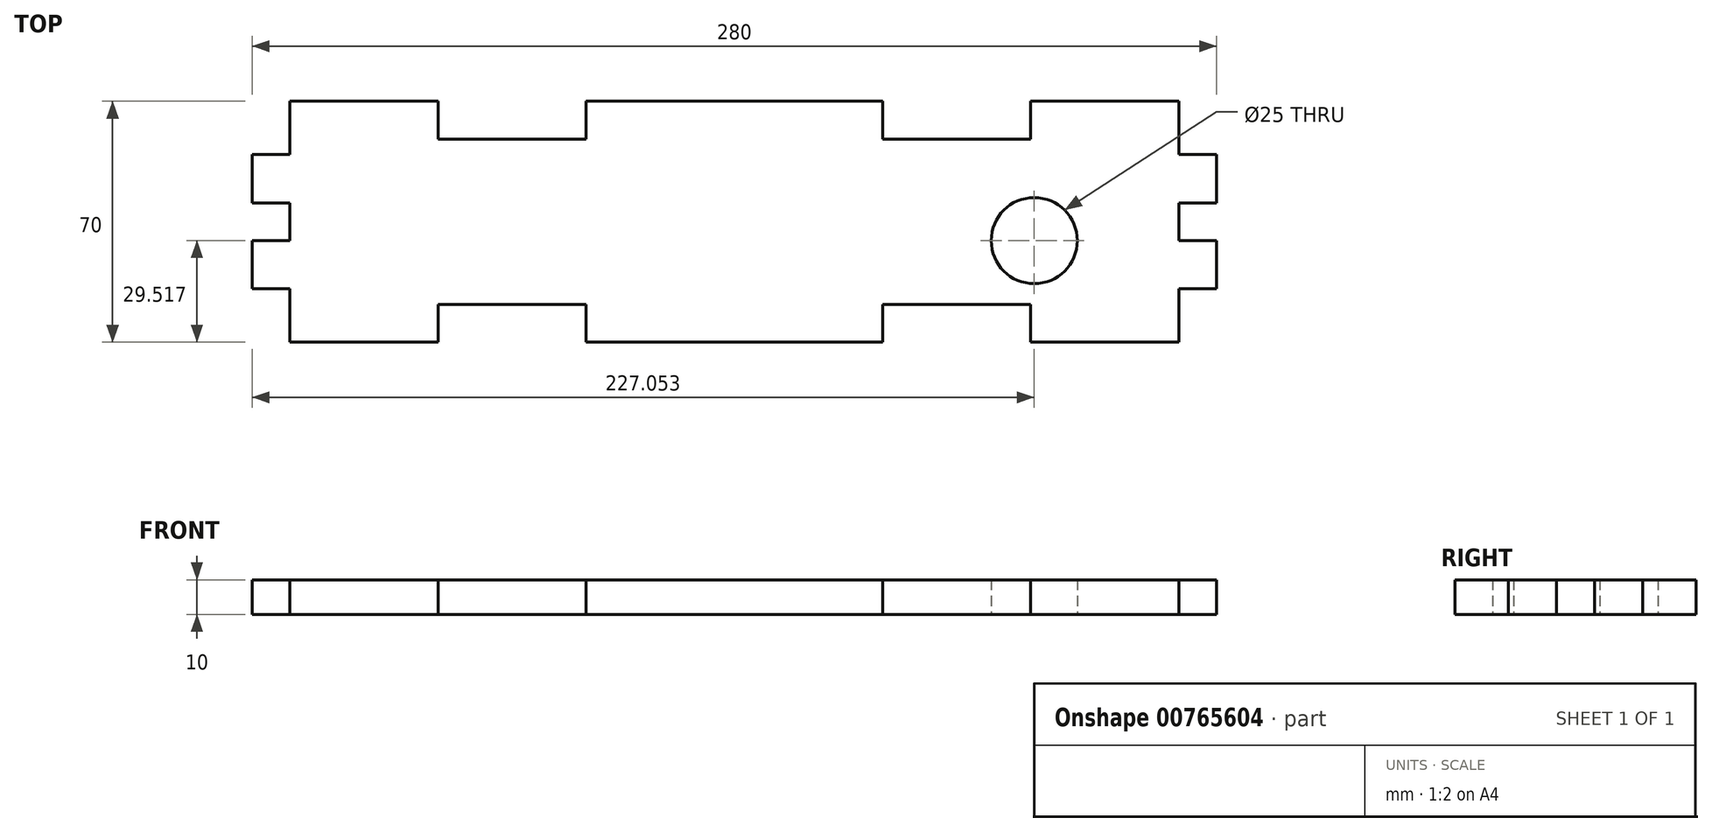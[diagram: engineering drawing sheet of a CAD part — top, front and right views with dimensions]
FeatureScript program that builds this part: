
annotation { "Feature Type Name" : "Feature", "Feature Type Description" : "" }
export const myFeature = defineFeature(function(context is Context, id is Id, definition is map)
    precondition{}
    {
        {
            var Q0;
            Q0=qCreatedBy(makeId("Top.planeOp"),FACE);
            var sketch = newSketch(context, id + "F0", { "sketchPlane" : qUnion([Q0])});
            skPoint(sketch, "E0.middle", {"position": v(0, 0) * mm});
            skLineSegment(sketch, "E1", {"start": v(129, 35) * mm, "end": v(129, 19.5) * mm});
            skLineSegment(sketch, "E2", {"start": v(129, 19.5) * mm, "end": v(140, 19.5) * mm});
            skLineSegment(sketch, "E3", {"start": v(140, 19.5) * mm, "end": v(140, 5.5) * mm});
            skLineSegment(sketch, "E4.MirrorCS", {"start": v(129, -35) * mm, "end": v(129, -19.5) * mm});
            skLineSegment(sketch, "E5.MirrorCS", {"start": v(129, -19.5) * mm, "end": v(140, -19.5) * mm});
            skLineSegment(sketch, "E6.MirrorCS", {"start": v(140, -19.5) * mm, "end": v(140, -5.5) * mm});
            skLineSegment(sketch, "E7", {"start": v(140, -5.5) * mm, "end": v(129, -5.5) * mm});
            skLineSegment(sketch, "E8", {"start": v(129, -5.5) * mm, "end": v(129, 5.5) * mm});
            skLineSegment(sketch, "E9", {"start": v(129, 5.5) * mm, "end": v(140, 5.5) * mm});
            skLineSegment(sketch, "E10.MirrorCS", {"start": v(-129, 35) * mm, "end": v(-129, 19.5) * mm});
            skLineSegment(sketch, "E11.MirrorCS", {"start": v(-129, 19.5) * mm, "end": v(-140, 19.5) * mm});
            skLineSegment(sketch, "E12.MirrorCS", {"start": v(-140, 19.5) * mm, "end": v(-140, 5.5) * mm});
            skLineSegment(sketch, "E13.MirrorCS", {"start": v(-129, 5.5) * mm, "end": v(-140, 5.5) * mm});
            skLineSegment(sketch, "E14.MirrorCS", {"start": v(-129, -5.5) * mm, "end": v(-129, 5.5) * mm});
            skLineSegment(sketch, "E15.MirrorCS", {"start": v(-140, -5.5) * mm, "end": v(-129, -5.5) * mm});
            skLineSegment(sketch, "E16.MirrorCS", {"start": v(-140, -19.5) * mm, "end": v(-140, -5.5) * mm});
            skLineSegment(sketch, "E17.MirrorCS", {"start": v(-129, -19.5) * mm, "end": v(-140, -19.5) * mm});
            skLineSegment(sketch, "E18.MirrorCS", {"start": v(-129, -35) * mm, "end": v(-129, -19.5) * mm});
            skLineSegment(sketch, "E19", {"start": v(-129, 35) * mm, "end": v(-86, 35) * mm});
            skLineSegment(sketch, "E20", {"start": v(-86, 35) * mm, "end": v(-86, 24) * mm});
            skLineSegment(sketch, "E21", {"start": v(-86, 24) * mm, "end": v(-43, 24) * mm});
            skLineSegment(sketch, "E22", {"start": v(-43, 24) * mm, "end": v(-43, 35) * mm});
            skLineSegment(sketch, "E23.MirrorCS", {"start": v(86, 35) * mm, "end": v(86, 24) * mm});
            skLineSegment(sketch, "E24.MirrorCS", {"start": v(86, 24) * mm, "end": v(43, 24) * mm});
            skLineSegment(sketch, "E25", {"start": v(86, 35) * mm, "end": v(129, 35) * mm});
            skLineSegment(sketch, "E26", {"start": v(43, 24) * mm, "end": v(43, 35) * mm});
            skLineSegment(sketch, "E27", {"start": v(-43, 35) * mm, "end": v(43, 35) * mm});
            skCircle(sketch, "E28", {"center": v(87.05, -5.48) * mm, "radius": 12.5 * mm});
            skLineSegment(sketch, "E29.MirrorCS", {"start": v(-129, -35) * mm, "end": v(-86, -35) * mm});
            skLineSegment(sketch, "E30.MirrorCS", {"start": v(-86, -35) * mm, "end": v(-86, -24) * mm});
            skLineSegment(sketch, "E31.MirrorCS", {"start": v(-86, -24) * mm, "end": v(-43, -24) * mm});
            skLineSegment(sketch, "E32.MirrorCS", {"start": v(-43, -24) * mm, "end": v(-43, -35) * mm});
            skLineSegment(sketch, "E33.MirrorCS", {"start": v(-43, -35) * mm, "end": v(43, -35) * mm});
            skLineSegment(sketch, "E34.MirrorCS", {"start": v(43, -24) * mm, "end": v(43, -35) * mm});
            skLineSegment(sketch, "E35.MirrorCS", {"start": v(86, -24) * mm, "end": v(43, -24) * mm});
            skLineSegment(sketch, "E36.MirrorCS", {"start": v(86, -35) * mm, "end": v(86, -24) * mm});
            skLineSegment(sketch, "E37.MirrorCS", {"start": v(86, -35) * mm, "end": v(129, -35) * mm});
            skSolve(sketch);
        }
        {
            var Q0;
            Q0=makeQuery(id+"F0.imprint","IMPRINT",FACE,{"disambiguationData":[TD([[makeQuery(id+"F0.imprint","IMPRINT",EDGE,{"derivedFrom":sQuery(id+"F0.wireOp",EDGE,"E1")}),-1.0]])]});
            extrude(context, id + "F1", {"entities" : qUnion([Q0]), "depth" : 10 * mm, "offsetDistance" : 25 * mm});
        }
    });
